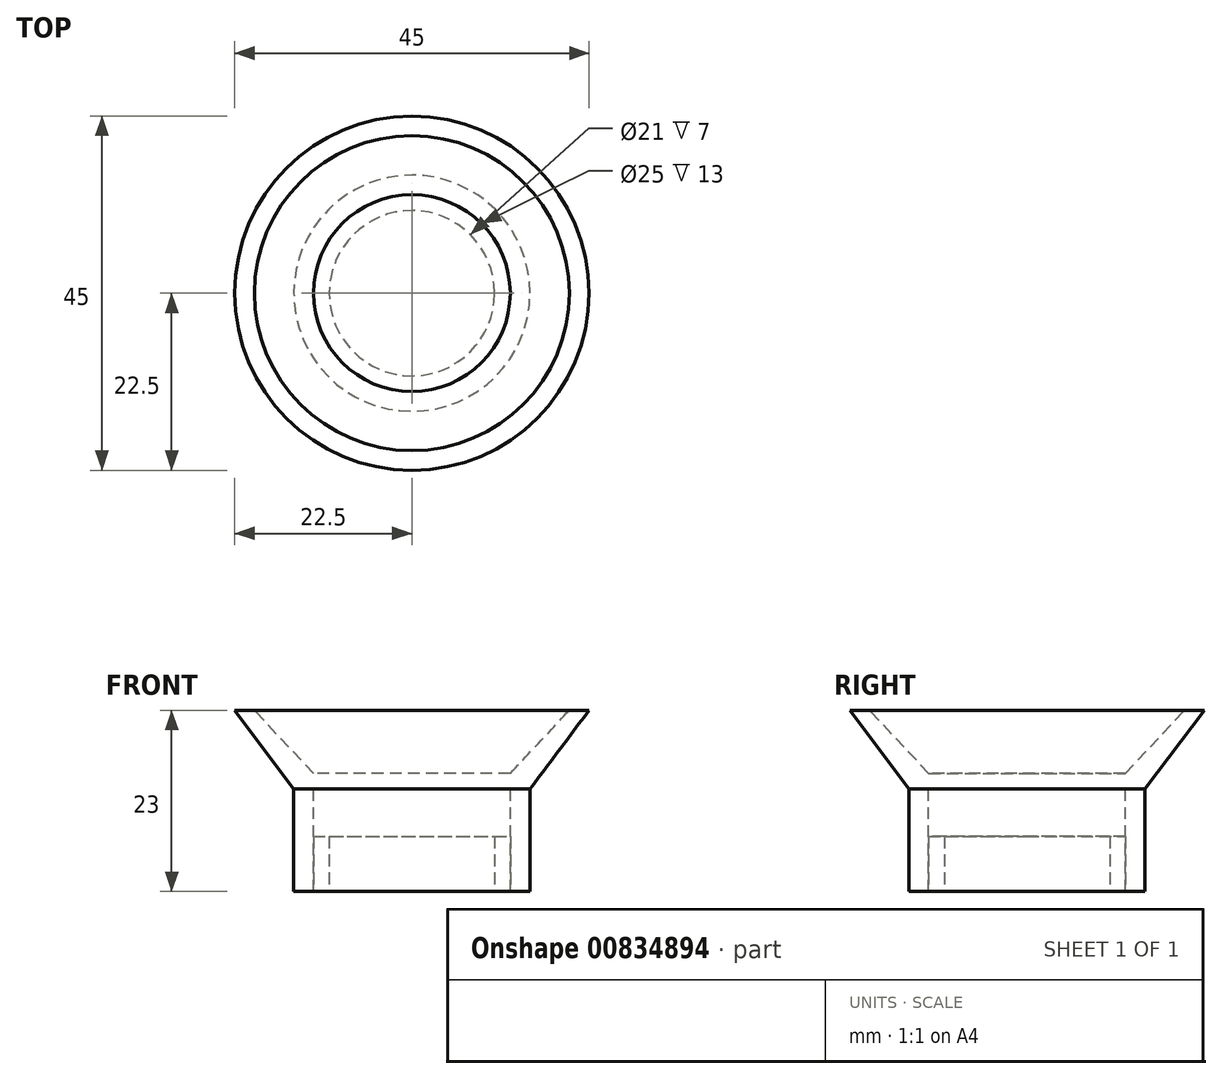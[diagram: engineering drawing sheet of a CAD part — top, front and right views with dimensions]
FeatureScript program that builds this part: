
annotation { "Feature Type Name" : "Feature", "Feature Type Description" : "" }
export const myFeature = defineFeature(function(context is Context, id is Id, definition is map)
    precondition{}
    {
        {
            var Q0;
            Q0=qCreatedBy(makeId("Top.planeOp"),FACE);
            var sketch = newSketch(context, id + "F0", { "sketchPlane" : qUnion([Q0])});
            skCircle(sketch, "E0", {"center": v(0, 0) * mm, "radius": 15 * mm});
            skSolve(sketch);
        }
        {
            var Q0;
            Q0=qCreatedBy(makeId("Top.planeOp"),FACE);
            cPlane(context, id + "F1", {"entities" : qUnion([Q0]), "cplaneType" : CPlaneType.OFFSET, "offset" : 10 * mm, "width" : 150 * mm, "height" : 150 * mm});
        }
        {
            var Q0;
            Q0=qCreatedBy(id+"F1.planeOp",FACE);
            var sketch = newSketch(context, id + "F2", { "sketchPlane" : qUnion([Q0])});
            skCircle(sketch, "E1", {"center": v(0, 0) * mm, "radius": 22.5 * mm});
            skSolve(sketch);
        }
        {
            var Q0;
            Q0 = qSketchRegion(id + "F0", true);
            var Q1;
            Q1 = qSketchRegion(id + "F2", true);
            loft(context, id + "F3", {"sheetProfilesArray" : [{ "sheetProfileEntities" : qUnion([Q0]) }, { "sheetProfileEntities" : qUnion([Q1]) }]});
        }
        {
            var Q0;
            Q0=makeQuery(id+"F3.opLoft","CAP_FACE",FACE,{"disambiguationData":[OSD([makeQuery(id+"F2.imprint","IMPRINT",FACE,{"disambiguationData":[TD([[makeQuery(id+"F2.imprint","IMPRINT",EDGE,{"derivedFrom":sQuery(id+"F2.wireOp",EDGE,"E1")}),1.0]])]})])],"isStart":true});
            var sketch = newSketch(context, id + "F4", { "sketchPlane" : qUnion([Q0])});
            skCircle(sketch, "E2", {"center": v(0, 0) * mm, "radius": 20 * mm});
            skSolve(sketch);
        }
        {
            var Q0;
            Q0=qCreatedBy(makeId("Top.planeOp"),FACE);
            cPlane(context, id + "F5", {"entities" : qUnion([Q0]), "cplaneType" : CPlaneType.OFFSET, "offset" : 2 * mm, "width" : 150 * mm, "height" : 150 * mm});
        }
        {
            var Q0;
            Q0=qCreatedBy(id+"F5.planeOp",FACE);
            var sketch = newSketch(context, id + "F6", { "sketchPlane" : qUnion([Q0])});
            skCircle(sketch, "E3", {"center": v(0, 0) * mm, "radius": 12.5 * mm});
            skSolve(sketch);
        }
        {
            var Q1;
            Q1 = qSketchRegion(id + "F4", true);
            var Q2;
            Q2 = qSketchRegion(id + "F6", true);
            loft(context, id + "F7", {"operationType" : NewBodyOperationType.REMOVE, "sheetProfilesArray" : [{ "sheetProfileEntities" : qUnion([Q1]) }, { "sheetProfileEntities" : qUnion([Q2]) }]});
        }
        {
            var Q0;
            Q0=makeQuery(id+"F3.opLoft","CAP_FACE",FACE,{"disambiguationData":[OSD([makeQuery(id+"F0.imprint","IMPRINT",FACE,{"disambiguationData":[TD([[makeQuery(id+"F0.imprint","IMPRINT",EDGE,{"derivedFrom":sQuery(id+"F0.wireOp",EDGE,"E0")}),1.0]])]})])],"isStart":true});
            var sketch = newSketch(context, id + "F8", { "sketchPlane" : qUnion([Q0])});
            skCircle(sketch, "E4", {"center": v(0, 0) * mm, "radius": 12.5 * mm});
            skSolve(sketch);
        }
        {
            var Q0;
            Q0=makeQuery(id+"F8.imprint","IMPRINT",FACE,{"disambiguationData":[TD([[makeQuery(id+"F8.imprint","IMPRINT",EDGE,{"derivedFrom":sQuery(id+"F8.wireOp",EDGE,"E4")}),-1.0]])]});
            extrude(context, id + "F9", {"entities" : qUnion([Q0]), "operationType" : NewBodyOperationType.ADD, "depth" : 13 * mm, "offsetDistance" : 25 * mm});
        }
        {
            var Q0;
            Q0=makeQuery(id+"F9.opExtrude","CAP_FACE",FACE,{"disambiguationData":[OSD([sQuery(id+"F0.wireOp",EDGE,"E0"),sQuery(id+"F8.wireOp",EDGE,"E4")])],"isStart":false});
            var sketch = newSketch(context, id + "F10", { "sketchPlane" : qUnion([Q0])});
            skCircle(sketch, "E5", {"center": v(0, 0) * mm, "radius": 12.5 * mm});
            skCircle(sketch, "E6", {"center": v(0, 0) * mm, "radius": 10.5 * mm});
            skSolve(sketch);
        }
        {
            var Q0;
            Q0 = qSketchRegion(id + "F10", true);
            extrude(context, id + "F11", {"entities" : qUnion([Q0]), "oppositeDirection" : true, "depth" : 7 * mm, "offsetDistance" : 25 * mm});
        }
        {
            var Q0;
            Q0=makeQuery(id+"F11.opExtrude","CAP_FACE",FACE,{"disambiguationData":[OSD([sQuery(id+"F10.wireOp",EDGE,"E5"),sQuery(id+"F10.wireOp",EDGE,"E6")])],"isStart":true});
            var sketch = newSketch(context, id + "F12", { "sketchPlane" : qUnion([Q0])});
            skCircle(sketch, "E7", {"center": v(0, 0) * mm, "radius": 15 * mm});
            skCircle(sketch, "E8", {"center": v(0, 0) * mm, "radius": 10.5 * mm});
            skSolve(sketch);
        }
        {
            var Q0;
            Q0=makeQuery(id+"F12.imprint","IMPRINT",FACE,{"disambiguationData":[TD([[makeQuery(id+"F12.imprint","IMPRINT",EDGE,{"derivedFrom":sQuery(id+"F12.wireOp",EDGE,"E7")}),1.0]])]});
            cPlane(context, id + "F13", {"entities" : qUnion([Q0]), "cplaneType" : CPlaneType.OFFSET, "offset" : 20 * mm, "width" : 150 * mm, "height" : 150 * mm});
        }
    });
